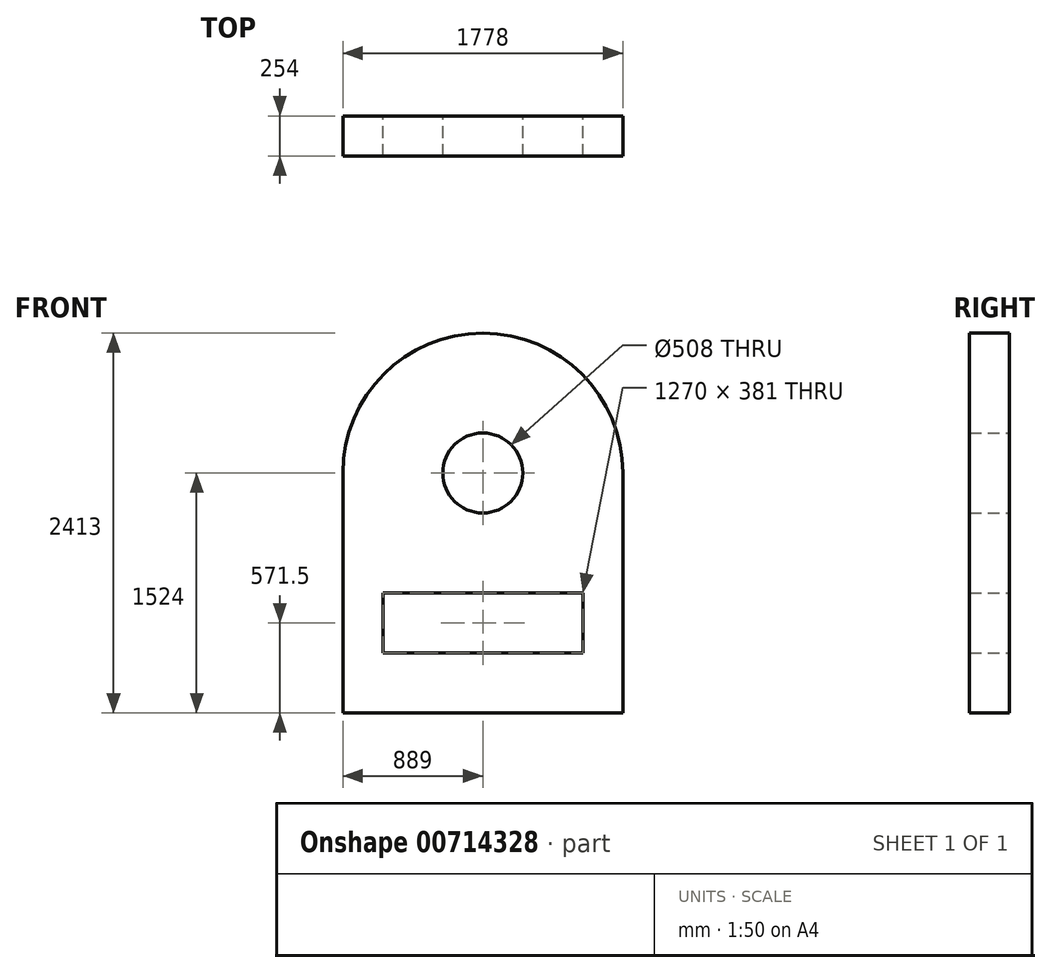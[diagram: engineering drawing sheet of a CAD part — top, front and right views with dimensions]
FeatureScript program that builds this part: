
annotation { "Feature Type Name" : "Feature", "Feature Type Description" : "" }
export const myFeature = defineFeature(function(context is Context, id is Id, definition is map)
    precondition{}
    {
        {
            var Q0;
            Q0=qCreatedBy(makeId("Front.planeOp"),FACE);
            var sketch = newSketch(context, id + "F0", { "sketchPlane" : qUnion([Q0])});
            skLineSegment(sketch, "E0", {"start": v(0, 0) * mm, "end": v(1778, 0) * mm});
            skLineSegment(sketch, "E1", {"start": v(0, 0) * mm, "end": v(0, 1524) * mm});
            skLineSegment(sketch, "E2", {"start": v(1778, 0) * mm, "end": v(1778, 1524) * mm});
            skArc(sketch, "E3", {"start": v(1778, 1524) * mm, "mid": v(889, 2413) * mm, "end": v(0, 1524) * mm});
            skCircle(sketch, "E4", {"center": v(889, 1524) * mm, "radius": 254 * mm});
            skLineSegment(sketch, "E5", {"start": v(254, 762) * mm, "end": v(1524, 762) * mm});
            skLineSegment(sketch, "E6", {"start": v(254, 762) * mm, "end": v(254, 381) * mm});
            skLineSegment(sketch, "E7", {"start": v(1524, 762) * mm, "end": v(1524, 381) * mm});
            skLineSegment(sketch, "E8", {"start": v(254, 381) * mm, "end": v(1524, 381) * mm});
            skSolve(sketch);
        }
        {
            var Q0;
            Q0=makeQuery(id+"F0.imprint","IMPRINT",FACE,{"disambiguationData":[TD([[makeQuery(id+"F0.imprint","IMPRINT",EDGE,{"derivedFrom":sQuery(id+"F0.wireOp",EDGE,"E0")}),1.0]])]});
            extrude(context, id + "F1", {"entities" : qUnion([Q0]), "depth" : 254 * mm, "offsetDistance" : 25.4 * mm});
        }
    });
